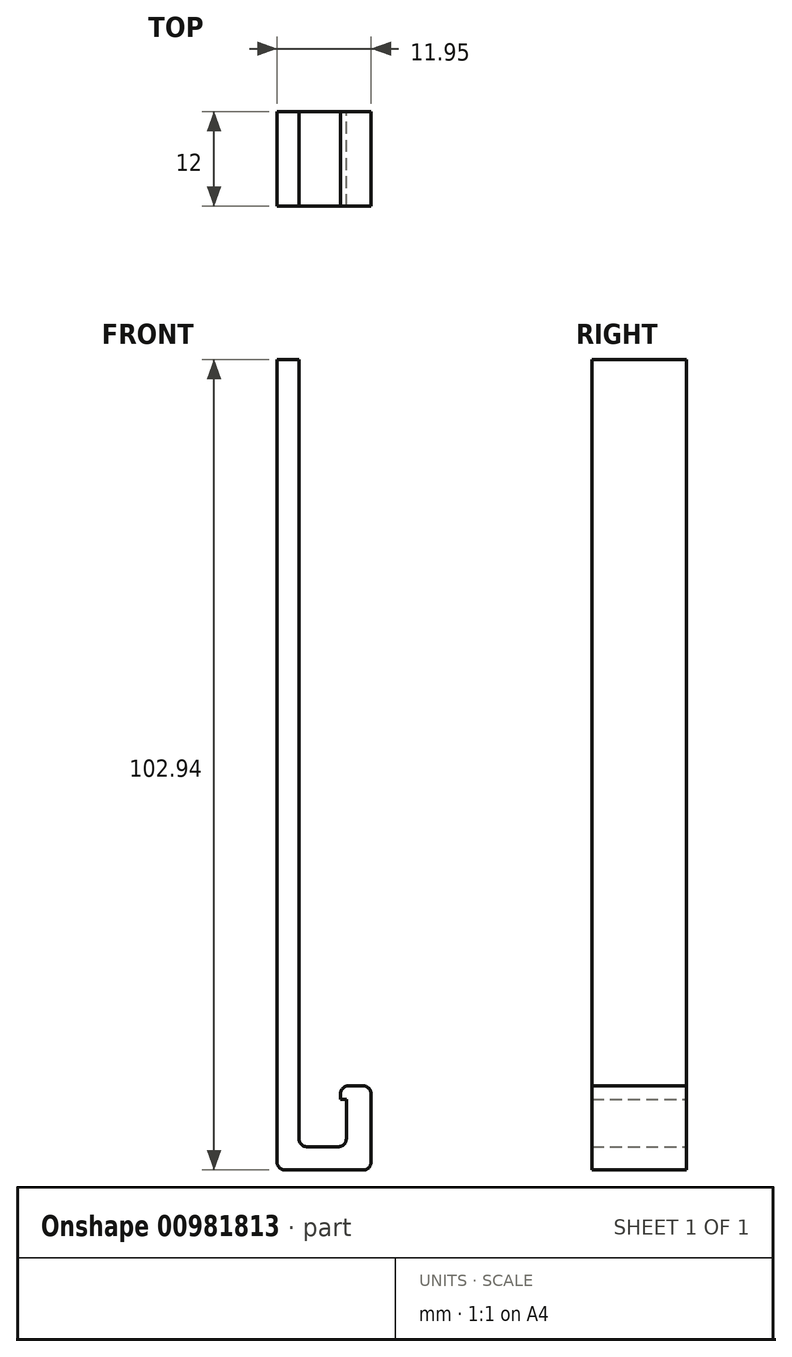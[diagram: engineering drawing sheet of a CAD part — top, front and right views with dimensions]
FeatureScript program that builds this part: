
annotation { "Feature Type Name" : "Feature", "Feature Type Description" : "" }
export const myFeature = defineFeature(function(context is Context, id is Id, definition is map)
    precondition{}
    {
        {
            var Q0;
            Q0=qCreatedBy(makeId("Front.planeOp"),FACE);
            var sketch = newSketch(context, id + "F0", { "sketchPlane" : qUnion([Q0])});
            skLineSegment(sketch, "E0.bottom", {"start": v(0, 86.94) * mm, "end": v(2.8, 86.94) * mm});
            skLineSegment(sketch, "E0.left", {"start": v(0, 86.94) * mm, "end": v(0, -13.06) * mm});
            skLineSegment(sketch, "E0.right", {"start": v(2.8, 86.94) * mm, "end": v(2.8, -12.06) * mm});
            skLineSegment(sketch, "E1", {"start": v(3.8, -13.06) * mm, "end": v(7.8, -13.06) * mm});
            skLineSegment(sketch, "E2", {"start": v(8.8, -12.06) * mm, "end": v(8.8, -7.06) * mm});
            skLineSegment(sketch, "E3", {"start": v(8.8, -7.06) * mm, "end": v(8.06, -7.06) * mm});
            skLineSegment(sketch, "E4", {"start": v(8.06, -7.06) * mm, "end": v(8.06, -6.33) * mm});
            skLineSegment(sketch, "E5", {"start": v(9.06, -5.33) * mm, "end": v(10.95, -5.33) * mm});
            skLineSegment(sketch, "E6", {"start": v(11.95, -6.33) * mm, "end": v(11.95, -13.06) * mm});
            skLineSegment(sketch, "E7", {"start": v(0, -13.06) * mm, "end": v(0, -15) * mm});
            skLineSegment(sketch, "E8", {"start": v(1, -16) * mm, "end": v(10.95, -16) * mm});
            skLineSegment(sketch, "E9", {"start": v(11.95, -15) * mm, "end": v(11.95, -13.06) * mm});
            skPoint(sketch, "E10.visualSharp", {"position": v(11.95, -16) * mm});
            skArc(sketch, "E10.filletArc", {"start": v(10.95, -16) * mm, "mid": v(11.66, -15.71) * mm, "end": v(11.95, -15) * mm});
            skPoint(sketch, "E11.visualSharp", {"position": v(0, -16) * mm});
            skArc(sketch, "E11.filletArc", {"start": v(0, -15) * mm, "mid": v(0.3, -15.71) * mm, "end": v(1, -16) * mm});
            skPoint(sketch, "E12.visualSharp", {"position": v(8.8, -13.06) * mm});
            skArc(sketch, "E12.filletArc", {"start": v(7.8, -13.06) * mm, "mid": v(8.5, -12.76) * mm, "end": v(8.8, -12.06) * mm});
            skPoint(sketch, "E13.visualSharp", {"position": v(2.8, -13.06) * mm});
            skArc(sketch, "E13.filletArc", {"start": v(2.8, -12.06) * mm, "mid": v(3.1, -12.76) * mm, "end": v(3.8, -13.06) * mm});
            skPoint(sketch, "E14.visualSharp", {"position": v(8.06, -5.33) * mm});
            skArc(sketch, "E14.filletArc", {"start": v(9.06, -5.33) * mm, "mid": v(8.36, -5.63) * mm, "end": v(8.06, -6.33) * mm});
            skPoint(sketch, "E15.visualSharp", {"position": v(11.95, -5.33) * mm});
            skArc(sketch, "E15.filletArc", {"start": v(11.95, -6.33) * mm, "mid": v(11.66, -5.63) * mm, "end": v(10.95, -5.33) * mm});
            skSolve(sketch);
        }
        {
            var Q0;
            Q0=makeQuery(id+"F0.imprint","IMPRINT",FACE,{"disambiguationData":[TD([[makeQuery(id+"F0.imprint","IMPRINT",EDGE,{"derivedFrom":sQuery(id+"F0.wireOp",EDGE,"E0.bottom")}),-1.0]])]});
            extrude(context, id + "F1", {"entities" : qUnion([Q0]), "depth" : 12 * mm, "offsetDistance" : 25 * mm});
        }
    });
